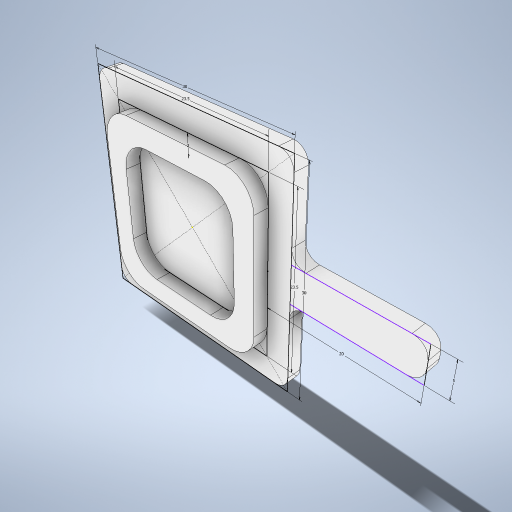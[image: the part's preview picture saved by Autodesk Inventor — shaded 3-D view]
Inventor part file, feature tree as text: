
AUTODESK INVENTOR PART (.ipt)
format: ipt  version: 2023 (Build 270158000, 158)  size: 310,784 bytes
history: native  units: mm
features: extrude x3, fillet x3, sketch x1
ambient origin geometry x8: Origin, YZ Plane, XZ Plane, XY Plane, X Axis, Y Axis, Z Axis, Center Point
bodies: Solid1 (feature_tree)
feature tree (7):
  sketch  "Sketch1"  dims[d0=30.0mm d1=30.0mm d2=23.5mm d3=23.5mm d4=3.0mm d7=2.0mm d8=0.0mm d10=5.0mm d12=20.0mm d13=2.0mm d14=0.0mm d15=2.0mm d16=2.0mm d17=2.0mm d18=0.0mm d19=4.0mm d20=0.0mm d21=0.0mm d22=0.0mm]
  extrude  "Extrusion2"  Depth=30.0mm
  extrude  "Extrusion3"  Depth=23.5mm
  fillet  "Fillet2"  Radius=23.5mm
  fillet  "Fillet3"  Radius=3.0mm
  extrude  "Extrusion4"  Depth=2.0mm TaperAngle=0.0deg
  fillet  "Fillet4"  Radius=5.0mm
